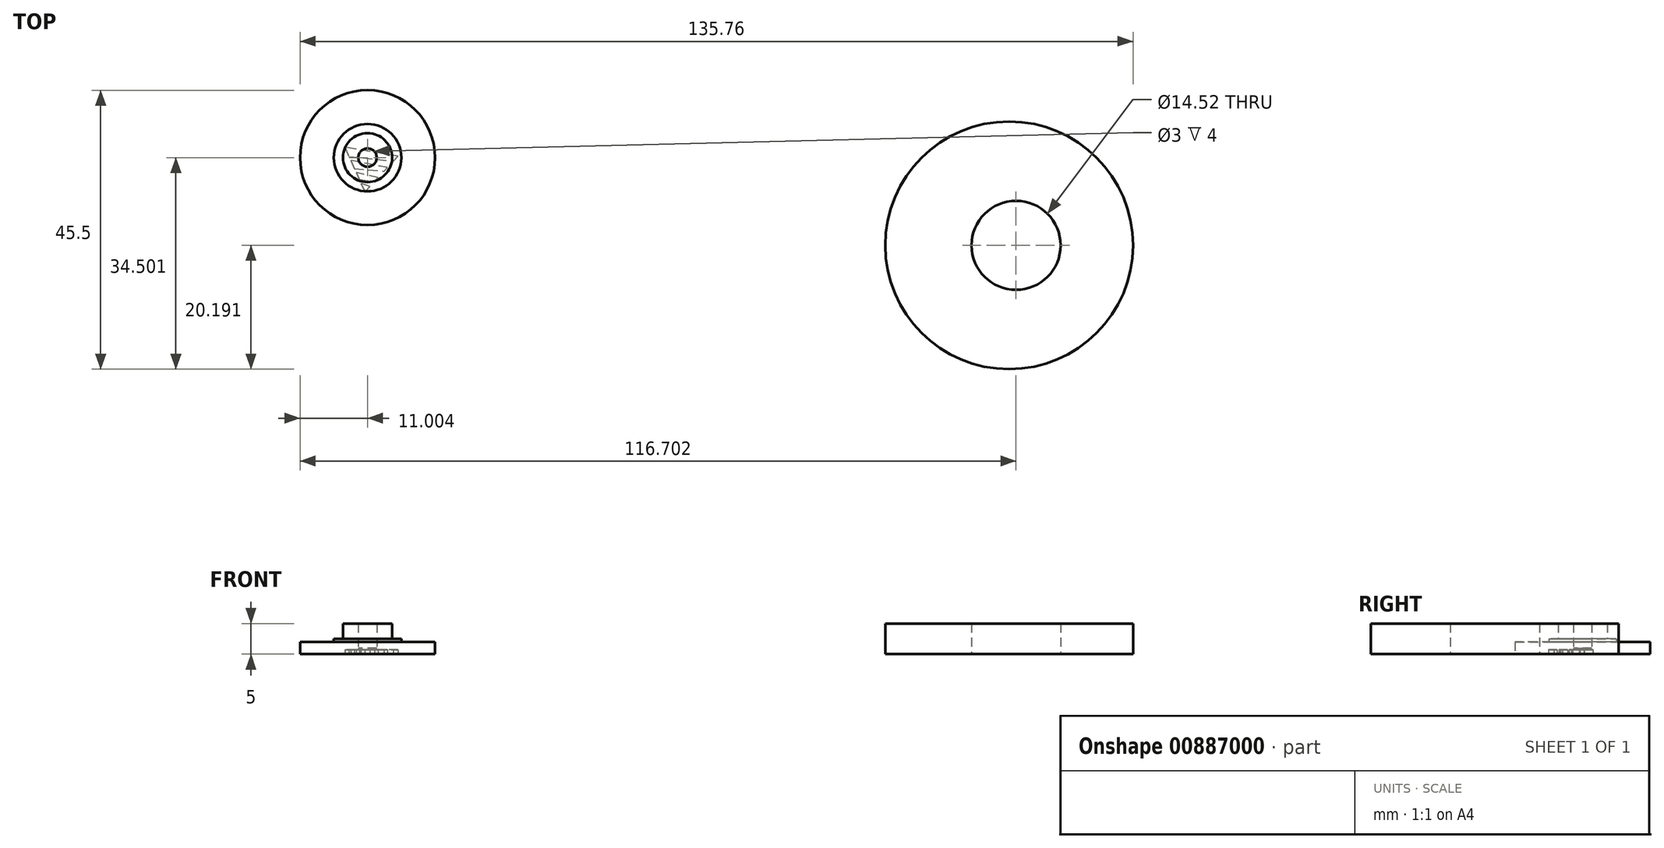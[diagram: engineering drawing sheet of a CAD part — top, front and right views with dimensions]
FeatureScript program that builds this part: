
annotation { "Feature Type Name" : "Feature", "Feature Type Description" : "" }
export const myFeature = defineFeature(function(context is Context, id is Id, definition is map)
    precondition{}
    {
        {
            var Q0;
            Q0=qCreatedBy(makeId("Top.planeOp"),FACE);
            var sketch = newSketch(context, id + "F0", { "sketchPlane" : qUnion([Q0])});
            skCircle(sketch, "E0", {"center": v(-59.49, 52.2) * mm, "radius": 4 * mm});
            skCircle(sketch, "E1", {"center": v(-59.49, 52.2) * mm, "radius": 1.5 * mm});
            skCircle(sketch, "E2", {"center": v(-59.49, 52.2) * mm, "radius": 11 * mm});
            skCircle(sketch, "E3", {"center": v(-59.49, 52.2) * mm, "radius": 5.5 * mm});
            skCircle(sketch, "E4", {"center": v(-131.05, 2.03) * mm, "radius": 4 * mm});
            skCircle(sketch, "E5", {"center": v(-131.05, 2.03) * mm, "radius": 1.5 * mm});
            skCircle(sketch, "E6", {"center": v(-131.05, 2.03) * mm, "radius": 11 * mm});
            skCircle(sketch, "E7", {"center": v(-131.05, 2.03) * mm, "radius": 5.5 * mm});
            skCircle(sketch, "E8", {"center": v(-131.05, -6.4) * mm, "radius": 1 * mm});
            skCircle(sketch, "E9.MirrorC", {"center": v(-131.05, 10.45) * mm, "radius": 1 * mm});
            skCircle(sketch, "E10.MirrorC", {"center": v(-139.47, 2.03) * mm, "radius": 1 * mm});
            skCircle(sketch, "E11.MirrorC", {"center": v(-122.62, 2.03) * mm, "radius": 1 * mm});
            skSolve(sketch);
        }
        {
            var Q0;
            Q0=makeQuery(id+"F0.imprint","IMPRINT",FACE,{"disambiguationData":[TD([[makeQuery(id+"F0.imprint","IMPRINT",EDGE,{"derivedFrom":sQuery(id+"F0.wireOp",EDGE,"E0")}),1.0]])]});
            extrude(context, id + "F1", {"entities" : qUnion([Q0]), "depth" : 5 * mm, "offsetDistance" : 25 * mm});
        }
        {
            var Q0;
            Q0=makeQuery(id+"F0.imprint","IMPRINT",FACE,{"disambiguationData":[TD([[makeQuery(id+"F0.imprint","IMPRINT",EDGE,{"derivedFrom":sQuery(id+"F0.wireOp",EDGE,"E0")}),-1.0]])]});
            extrude(context, id + "F2", {"entities" : qUnion([Q0]), "operationType" : NewBodyOperationType.ADD, "depth" : 2.5 * mm, "offsetDistance" : 25 * mm});
        }
        {
            var Q0;
            Q0=makeQuery(id+"F0.imprint","IMPRINT",FACE,{"disambiguationData":[TD([[makeQuery(id+"F0.imprint","IMPRINT",EDGE,{"derivedFrom":sQuery(id+"F0.wireOp",EDGE,"E2")}),1.0]])]});
            extrude(context, id + "F3", {"entities" : qUnion([Q0]), "operationType" : NewBodyOperationType.ADD, "depth" : 2 * mm, "offsetDistance" : 25 * mm});
        }
        {
            var Q0;
            {var subQ0=sQuery(id+"F0.wireOp",EDGE,"E3");var subQ1=sQuery(id+"F0.wireOp",EDGE,"E0");Q0=makeQuery(id+"F3.boolean.opBoolean","MERGE",FACE,{"derivedFrom":[makeQuery(id+"F2.boolean.opBoolean","MERGE",FACE,{"derivedFrom":[makeQuery(id+"F1.opExtrude","CAP_FACE",FACE,{"disambiguationData":[OSD([subQ1,sQuery(id+"F0.wireOp",EDGE,"E1")])],"isStart":true}),makeQuery(id+"F2.opExtrude","CAP_FACE",FACE,{"disambiguationData":[OSD([subQ1,subQ0])],"isStart":true})]}),makeQuery(id+"F3.opExtrude","CAP_FACE",FACE,{"disambiguationData":[OSD([sQuery(id+"F0.wireOp",EDGE,"E2"),subQ0,sQuery(id+"F0.wireOp",EDGE,"a77LPZrQ-2fYS-kDON-aBan-clsV7zol38i9"),sQuery(id+"F0.wireOp",EDGE,"e731c295-62d8-4e5b-a4ae-7bbec1b443e30.MirrorC"),sQuery(id+"F0.wireOp",EDGE,"690bf0c8-3db3-4080-9a09-63a28f12edb30.MirrorC"),sQuery(id+"F0.wireOp",EDGE,"bd635ff9-f126-4287-8758-d050c94f3a850.MirrorC")])],"isStart":true})]});}
            var sketch = newSketch(context, id + "F4", { "sketchPlane" : qUnion([Q0])});
            skCircle(sketch, "E12", {"center": v(-59.49, -52.2) * mm, "radius": 1.5 * mm});
            skSolve(sketch);
        }
        {
            var Q0;
            Q0=makeQuery(id+"F4.imprint","IMPRINT",FACE,{"disambiguationData":[TD([[makeQuery(id+"F4.imprint","IMPRINT",EDGE,{"derivedFrom":sQuery(id+"F4.wireOp",EDGE,"E12")}),-1.0]])]});
            extrude(context, id + "F5", {"entities" : qUnion([Q0]), "oppositeDirection" : true, "depth" : 1 * mm, "offsetDistance" : 25 * mm});
        }
        {
            var Q0;
            Q0=makeQuery(id+"F1.opExtrude","SWEPT_BODY",BODY,{"disambiguationData":[OSD([sQuery(id+"F0.wireOp",EDGE,"E0"),sQuery(id+"F0.wireOp",EDGE,"E1")])]});
            var Q1;
            Q1=makeQuery(id+"F5.opExtrude","SWEPT_BODY",BODY,{"disambiguationData":[OSD([sQuery(id+"F4.wireOp",EDGE,"E12")])]});
            booleanBodies(context, id + "F6", {"operationType" : BooleanOperationType.UNION, "tools" : qUnion([Q0, Q1])});
        }
        {
            var Q0;
            {var subQ0=sQuery(id+"F0.wireOp",EDGE,"E3");var subQ1=sQuery(id+"F0.wireOp",EDGE,"E0");Q0=makeQuery(id+"F6.opBoolean","MERGE",FACE,{"derivedFrom":[makeQuery(id+"F3.boolean.opBoolean","MERGE",FACE,{"derivedFrom":[makeQuery(id+"F2.boolean.opBoolean","MERGE",FACE,{"derivedFrom":[makeQuery(id+"F1.opExtrude","CAP_FACE",FACE,{"disambiguationData":[OSD([subQ1,sQuery(id+"F0.wireOp",EDGE,"E1")])],"isStart":true}),makeQuery(id+"F2.opExtrude","CAP_FACE",FACE,{"disambiguationData":[OSD([subQ1,subQ0])],"isStart":true})]}),makeQuery(id+"F3.opExtrude","CAP_FACE",FACE,{"disambiguationData":[OSD([sQuery(id+"F0.wireOp",EDGE,"E2"),subQ0])],"isStart":true})]}),makeQuery(id+"F5.opExtrude","CAP_FACE",FACE,{"disambiguationData":[OSD([sQuery(id+"F4.wireOp",EDGE,"E12")])],"isStart":true})]});}
            var sketch = newSketch(context, id + "F7", { "sketchPlane" : qUnion([Q0])});
            skLineSegment(sketch, "E13", {"start": v(-63.18, -53.88) * mm, "end": v(-62.52, -52.4) * mm});
            skLineSegment(sketch, "E14", {"start": v(-59.94, -46.6) * mm, "end": v(-59.1, -47.5) * mm});
            skLineSegment(sketch, "E15", {"start": v(-54.52, -52.44) * mm, "end": v(-63.18, -53.88) * mm});
            skLineSegment(sketch, "E16", {"start": v(-62.52, -52.4) * mm, "end": v(-55.29, -51.61) * mm});
            skLineSegment(sketch, "E17", {"start": v(-56.25, -50.57) * mm, "end": v(-62.23, -51.74) * mm});
            skLineSegment(sketch, "E18", {"start": v(-61.63, -50.4) * mm, "end": v(-56.81, -49.97) * mm});
            skLineSegment(sketch, "E19", {"start": v(-57.8, -48.9) * mm, "end": v(-61.35, -49.76) * mm});
            skLineSegment(sketch, "E20", {"start": v(-60.83, -48.6) * mm, "end": v(-58.32, -48.35) * mm});
            skLineSegment(sketch, "E21", {"start": v(-59.1, -47.5) * mm, "end": v(-60.56, -48) * mm});
            skLineSegment(sketch, "E22.trimOffspring", {"start": v(-58.32, -48.35) * mm, "end": v(-57.8, -48.9) * mm});
            skLineSegment(sketch, "E23.trimOffspring", {"start": v(-60.56, -48) * mm, "end": v(-59.94, -46.6) * mm});
            skLineSegment(sketch, "E24.trimOffspring", {"start": v(-56.81, -49.97) * mm, "end": v(-56.25, -50.57) * mm});
            skLineSegment(sketch, "E25.trimOffspring", {"start": v(-61.35, -49.76) * mm, "end": v(-60.83, -48.6) * mm});
            skLineSegment(sketch, "E26.trimOffspring", {"start": v(-55.29, -51.61) * mm, "end": v(-54.52, -52.44) * mm});
            skLineSegment(sketch, "E27.trimOffspring", {"start": v(-62.23, -51.74) * mm, "end": v(-61.63, -50.4) * mm});
            skSolve(sketch);
        }
        {
            var Q0;
            Q0 = qSketchRegion(id + "F7", true);
            extrude(context, id + "F8", {"entities" : qUnion([Q0]), "operationType" : NewBodyOperationType.REMOVE, "oppositeDirection" : true, "depth" : .75 * mm, "offsetDistance" : 25 * mm});
        }
        {
            var Q0;
            Q0=qCreatedBy(makeId("Top.planeOp"),FACE);
            var sketch = newSketch(context, id + "F9", { "sketchPlane" : qUnion([Q0])});
            skCircle(sketch, "E28", {"center": v(45.08, 37.88) * mm, "radius": 20.2 * mm});
            skCircle(sketch, "E29", {"center": v(46.21, 37.88) * mm, "radius": 7.26 * mm});
            skSolve(sketch);
        }
        {
            var Q0;
            Q0=makeQuery(id+"F9.imprint","IMPRINT",FACE,{"disambiguationData":[TD([[makeQuery(id+"F9.imprint","IMPRINT",EDGE,{"derivedFrom":sQuery(id+"F9.wireOp",EDGE,"E28")}),1.0]])]});
            extrude(context, id + "F10", {"entities" : qUnion([Q0]), "depth" : 5 * mm, "offsetDistance" : 25 * mm});
        }
    });
